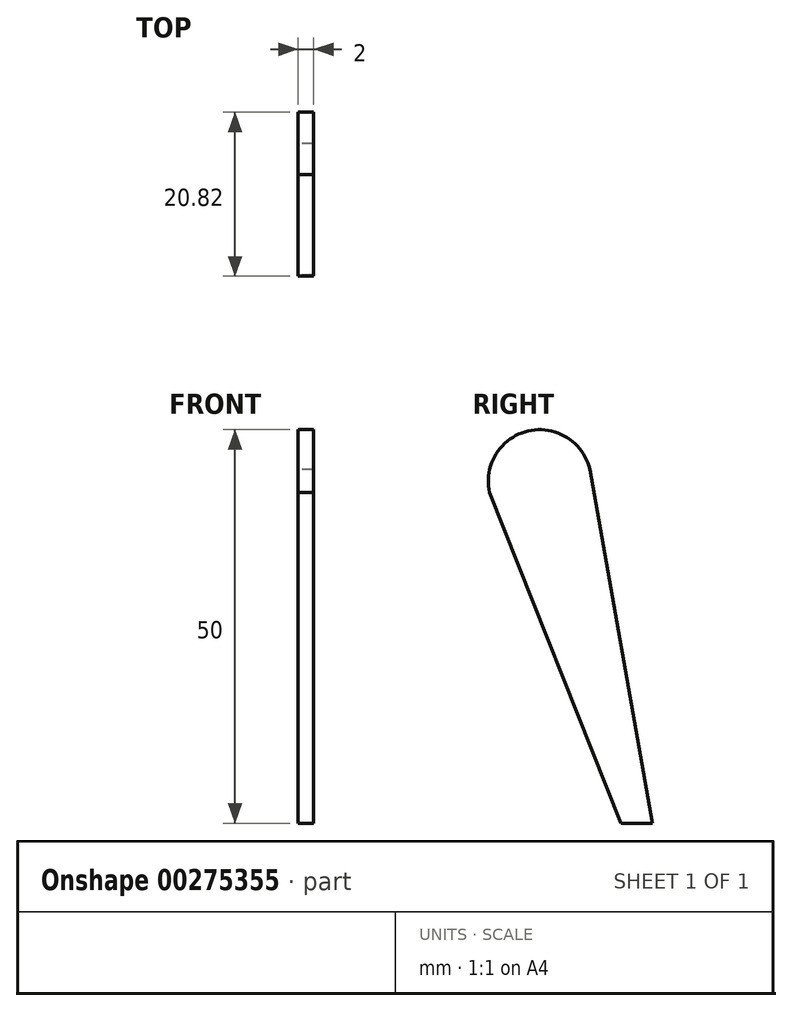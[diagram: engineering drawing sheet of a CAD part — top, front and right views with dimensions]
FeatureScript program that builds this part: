
annotation { "Feature Type Name" : "Feature", "Feature Type Description" : "" }
export const myFeature = defineFeature(function(context is Context, id is Id, definition is map)
    precondition{}
    {
        {
            var Q0;
            Q0=qCreatedBy(makeId("Right.planeOp"),FACE);
            var sketch = newSketch(context, id + "F0", { "sketchPlane" : qUnion([Q0])});
            skLineSegment(sketch, "E0", {"start": v(25, 4) * mm, "end": v(33.82, -46) * mm});
            skLineSegment(sketch, "E1", {"start": v(33.82, -46) * mm, "end": v(29.82, -46) * mm});
            skLineSegment(sketch, "E2", {"start": v(29.82, -46) * mm, "end": v(13.17, -4) * mm});
            skLineSegment(sketch, "E3", {"start": v(13.17, -4) * mm, "end": v(0, -4) * mm});
            skLineSegment(sketch, "E4", {"start": v(0, -4) * mm, "end": v(0, 4) * mm, "construction": true});
            skLineSegment(sketch, "E5", {"start": v(13.17, -4) * mm, "end": v(10, 4) * mm, "construction": true});
            skLineSegment(sketch, "E6", {"start": v(0, 4) * mm, "end": v(10, 4) * mm});
            skLineSegment(sketch, "E7", {"start": v(25, 4) * mm, "end": v(10, 4) * mm});
            skLineSegment(sketch, "E8.MirrorCS", {"start": v(0, 4) * mm, "end": v(-10, 4) * mm});
            skLineSegment(sketch, "E9.MirrorCS", {"start": v(-25, 4) * mm, "end": v(-10, 4) * mm});
            skLineSegment(sketch, "E10.MirrorCS", {"start": v(-13.17, -4) * mm, "end": v(0, -4) * mm});
            skLineSegment(sketch, "E11.MirrorCS", {"start": v(-13.17, -4) * mm, "end": v(-10, 4) * mm, "construction": true});
            skLineSegment(sketch, "E12.MirrorCS", {"start": v(-29.82, -46) * mm, "end": v(-13.17, -4) * mm});
            skLineSegment(sketch, "E13.MirrorCS", {"start": v(-25, 4) * mm, "end": v(-33.82, -46) * mm});
            skLineSegment(sketch, "E14.MirrorCS", {"start": v(-33.82, -46) * mm, "end": v(-29.82, -46) * mm});
            skSolve(sketch);
        }
        {
            var Q0;
            Q0=qCreatedBy(makeId("Right.planeOp"),FACE);
            var sketch = newSketch(context, id + "F1", { "sketchPlane" : qUnion([Q0])});
            skLineSegment(sketch, "E15", {"start": v(25, 4) * mm, "end": v(33.82, -46) * mm});
            skLineSegment(sketch, "E16", {"start": v(33.82, -46) * mm, "end": v(29.82, -46) * mm});
            skLineSegment(sketch, "E17", {"start": v(29.82, -46) * mm, "end": v(13.17, -4) * mm});
            skLineSegment(sketch, "E18", {"start": v(13.17, -4) * mm, "end": v(0, -4) * mm, "construction": true});
            skLineSegment(sketch, "E19", {"start": v(0, -4) * mm, "end": v(0, 4) * mm, "construction": true});
            skLineSegment(sketch, "E20", {"start": v(13.17, -4) * mm, "end": v(10, 4) * mm, "construction": true});
            skLineSegment(sketch, "E21", {"start": v(0, 4) * mm, "end": v(10, 4) * mm, "construction": true});
            skLineSegment(sketch, "E22", {"start": v(25, 4) * mm, "end": v(10, 4) * mm, "construction": true});
            skArc(sketch, "E23", {"start": v(25.9, -1.06) * mm, "mid": v(18.06, 3.83) * mm, "end": v(13.17, -4) * mm});
            skLineSegment(sketch, "E24", {"start": v(13.17, -4) * mm, "end": v(25.9, -1.06) * mm, "construction": true});
            skSolve(sketch);
        }
        {
            var Q0;
            {var subQ0=sQuery(id+"F1.wireOp",EDGE,"E16");Q0=makeQuery(id+"F1.imprint","IMPRINT",FACE,{"disambiguationData":[TD([[makeQuery(id+"F1.imprint","IMPRINT",EDGE,{"derivedFrom":subQ0}),-1.0]])]});}
            extrude(context, id + "F2", {"entities" : qUnion([Q0]), "depth" : 2 * mm, "offsetDistance" : 25 * mm});
        }
    });
